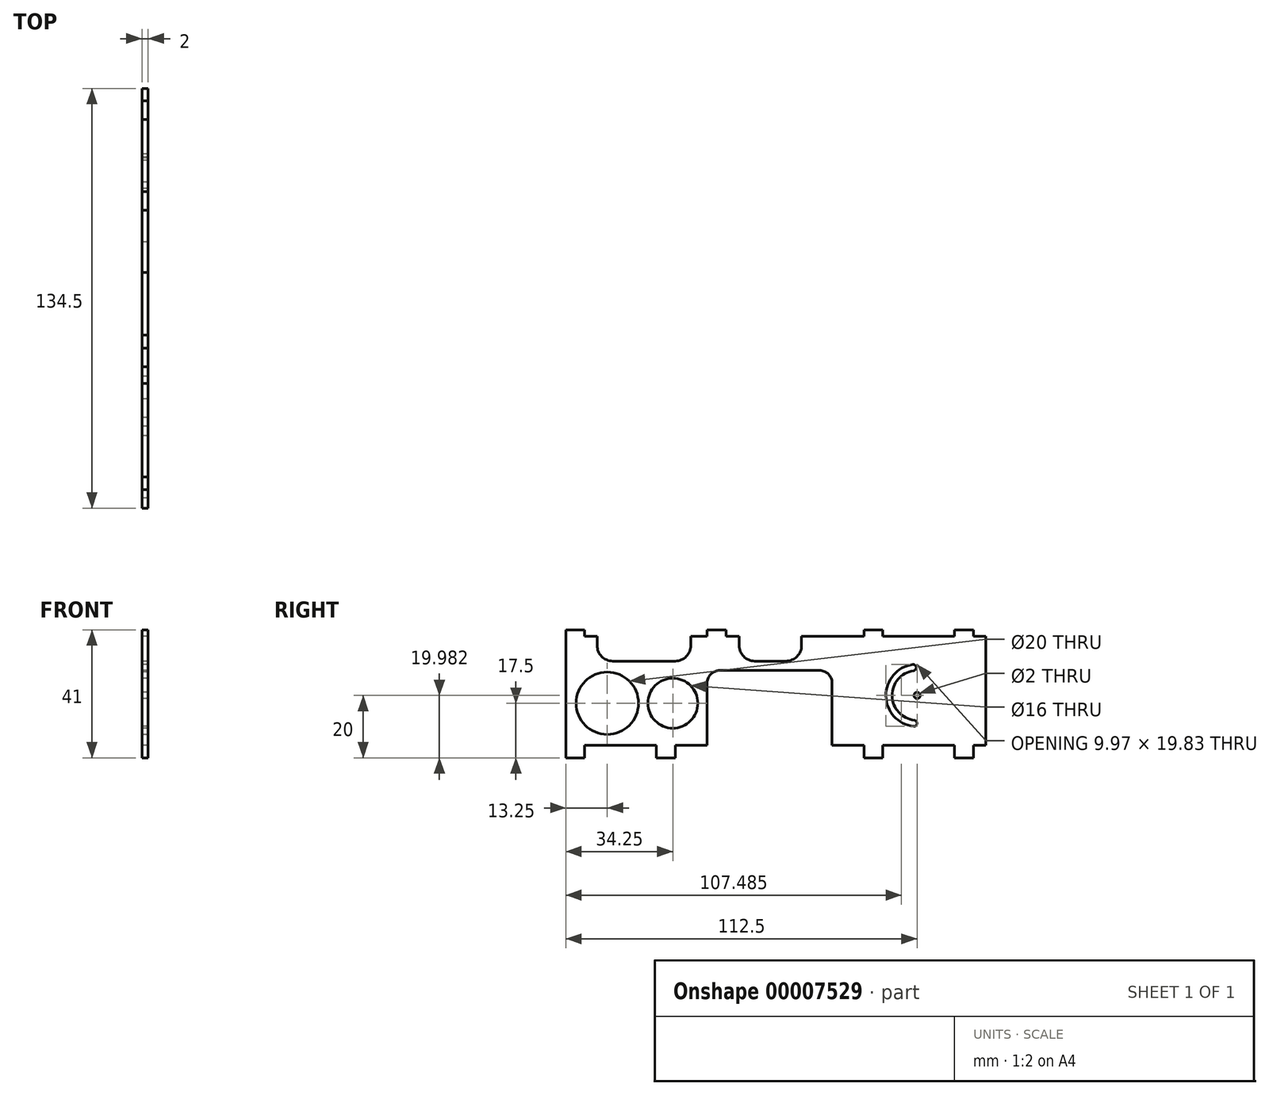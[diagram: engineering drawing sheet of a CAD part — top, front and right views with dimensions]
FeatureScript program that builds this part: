
annotation { "Feature Type Name" : "Feature", "Feature Type Description" : "" }
export const myFeature = defineFeature(function(context is Context, id is Id, definition is map)
    precondition{}
    {
        {
            var Q0;
            Q0=qCreatedBy(makeId("Right.planeOp"),FACE);
            var sketch = newSketch(context, id + "F0", { "sketchPlane" : qUnion([Q0])});
            skLineSegment(sketch, "E0.bottom", {"start": v(65.25, 0) * mm, "end": v(-65.25, 0) * mm});
            skLineSegment(sketch, "E0.top", {"start": v(65.25, 41) * mm, "end": v(-65.25, 41) * mm});
            skLineSegment(sketch, "E0.left", {"start": v(65.25, 0) * mm, "end": v(65.25, 41) * mm});
            skLineSegment(sketch, "E0.right", {"start": v(-65.25, 0) * mm, "end": v(-65.25, 41) * mm});
            skLineSegment(sketch, "E1.bottom", {"start": v(-59.25, 0) * mm, "end": v(-36.25, 0) * mm});
            skLineSegment(sketch, "E1.top", {"start": v(-59.25, 4) * mm, "end": v(-36.25, 4) * mm});
            skLineSegment(sketch, "E1.left", {"start": v(-59.25, 0) * mm, "end": v(-59.25, 4) * mm});
            skLineSegment(sketch, "E1.right", {"start": v(-36.25, 0) * mm, "end": v(-36.25, 4) * mm});
            skLineSegment(sketch, "E2.bottom", {"start": v(-20, 0) * mm, "end": v(20, 0) * mm});
            skLineSegment(sketch, "E2.top", {"start": v(-16, 28) * mm, "end": v(16, 28) * mm});
            skLineSegment(sketch, "E2.left", {"start": v(-20, 0) * mm, "end": v(-20, 24) * mm});
            skLineSegment(sketch, "E2.right", {"start": v(20, 0) * mm, "end": v(20, 24) * mm});
            skLineSegment(sketch, "E3.bottom", {"start": v(36.25, 0) * mm, "end": v(59.25, 0) * mm});
            skLineSegment(sketch, "E3.top", {"start": v(36.25, 4) * mm, "end": v(59.25, 4) * mm});
            skLineSegment(sketch, "E3.left", {"start": v(36.25, 0) * mm, "end": v(36.25, 4) * mm});
            skLineSegment(sketch, "E3.right", {"start": v(59.25, 0) * mm, "end": v(59.25, 4) * mm});
            skLineSegment(sketch, "E4.bottom", {"start": v(-30.25, 0) * mm, "end": v(-20, 0) * mm});
            skLineSegment(sketch, "E4.top", {"start": v(-30.25, 4) * mm, "end": v(-20, 4) * mm});
            skLineSegment(sketch, "E4.left", {"start": v(-30.25, 0) * mm, "end": v(-30.25, 4) * mm});
            skLineSegment(sketch, "E4.right", {"start": v(-20, 0) * mm, "end": v(-20, 4) * mm});
            skLineSegment(sketch, "E5.bottom", {"start": v(20, 0) * mm, "end": v(30.25, 0) * mm});
            skLineSegment(sketch, "E5.top", {"start": v(20, 4) * mm, "end": v(30.25, 4) * mm});
            skLineSegment(sketch, "E5.left", {"start": v(20, 0) * mm, "end": v(20, 4) * mm});
            skLineSegment(sketch, "E5.right", {"start": v(30.25, 0) * mm, "end": v(30.25, 4) * mm});
            skLineSegment(sketch, "E6.bottom", {"start": v(65.25, 41) * mm, "end": v(59.25, 41) * mm});
            skLineSegment(sketch, "E6.top", {"start": v(65.25, 39) * mm, "end": v(59.25, 39) * mm});
            skLineSegment(sketch, "E6.left", {"start": v(65.25, 41) * mm, "end": v(65.25, 39) * mm});
            skLineSegment(sketch, "E6.right", {"start": v(59.25, 41) * mm, "end": v(59.25, 39) * mm});
            skLineSegment(sketch, "E7.bottom", {"start": v(-20, 41) * mm, "end": v(-14, 41) * mm});
            skLineSegment(sketch, "E7.top", {"start": v(-20, 39) * mm, "end": v(-14, 39) * mm});
            skLineSegment(sketch, "E7.left", {"start": v(-20, 41) * mm, "end": v(-20, 39) * mm});
            skLineSegment(sketch, "E7.right", {"start": v(-14, 41) * mm, "end": v(-14, 39) * mm});
            skLineSegment(sketch, "E8.bottom", {"start": v(-65.25, 41) * mm, "end": v(-59.25, 41) * mm});
            skLineSegment(sketch, "E8.top", {"start": v(-65.25, 39) * mm, "end": v(-59.25, 39) * mm});
            skLineSegment(sketch, "E8.left", {"start": v(-65.25, 41) * mm, "end": v(-65.25, 39) * mm});
            skLineSegment(sketch, "E8.right", {"start": v(-59.25, 41) * mm, "end": v(-59.25, 39) * mm});
            skPoint(sketch, "E9.visualSharp", {"position": v(-20, 28) * mm});
            skArc(sketch, "E9.filletArc", {"start": v(-16, 28) * mm, "mid": v(-18.83, 26.83) * mm, "end": v(-20, 24) * mm});
            skPoint(sketch, "E10.visualSharp", {"position": v(20, 28) * mm});
            skArc(sketch, "E10.filletArc", {"start": v(20, 24) * mm, "mid": v(18.83, 26.83) * mm, "end": v(16, 28) * mm});
            skLineSegment(sketch, "E11.bottom", {"start": v(65.25, 39) * mm, "end": v(69.25, 39) * mm});
            skLineSegment(sketch, "E11.top", {"start": v(65.25, 4) * mm, "end": v(69.25, 4) * mm});
            skLineSegment(sketch, "E11.left", {"start": v(65.25, 39) * mm, "end": v(65.25, 4) * mm});
            skLineSegment(sketch, "E11.right", {"start": v(69.25, 39) * mm, "end": v(69.25, 4) * mm});
            skCircle(sketch, "E12", {"center": v(47.25, 20) * mm, "radius": 1 * mm});
            skArc(sketch, "E13", {"start": v(45.83, 29.9) * mm, "mid": v(37.25, 19.86) * mm, "end": v(46.11, 10.06) * mm});
            skArc(sketch, "E14.0", {"start": v(46.11, 27.92) * mm, "mid": v(39.25, 19.88) * mm, "end": v(46.34, 12.05) * mm});
            skArc(sketch, "E15", {"start": v(46.11, 10.06) * mm, "mid": v(47.22, 10.94) * mm, "end": v(46.34, 12.05) * mm});
            skArc(sketch, "E16", {"start": v(46.11, 27.92) * mm, "mid": v(46.96, 29.05) * mm, "end": v(45.83, 29.9) * mm});
            skLineSegment(sketch, "E17.bottom", {"start": v(-55.25, 41) * mm, "end": v(-25.25, 41) * mm});
            skLineSegment(sketch, "E17.top", {"start": v(-50.25, 31) * mm, "end": v(-30.25, 31) * mm});
            skLineSegment(sketch, "E17.left", {"start": v(-55.25, 41) * mm, "end": v(-55.25, 36) * mm});
            skLineSegment(sketch, "E17.right", {"start": v(-25.25, 41) * mm, "end": v(-25.25, 36) * mm});
            skLineSegment(sketch, "E18.bottom", {"start": v(-9.75, 41) * mm, "end": v(10.25, 41) * mm});
            skLineSegment(sketch, "E18.top", {"start": v(-4.75, 31) * mm, "end": v(5.25, 31) * mm});
            skLineSegment(sketch, "E18.left", {"start": v(-9.75, 41) * mm, "end": v(-9.75, 36) * mm});
            skLineSegment(sketch, "E18.right", {"start": v(10.25, 41) * mm, "end": v(10.25, 36) * mm});
            skPoint(sketch, "E19.visualSharp", {"position": v(-55.25, 31) * mm});
            skArc(sketch, "E19.filletArc", {"start": v(-55.25, 36) * mm, "mid": v(-53.79, 32.46) * mm, "end": v(-50.25, 31) * mm});
            skPoint(sketch, "E20.visualSharp", {"position": v(-25.25, 31) * mm});
            skArc(sketch, "E20.filletArc", {"start": v(-30.25, 31) * mm, "mid": v(-26.71, 32.46) * mm, "end": v(-25.25, 36) * mm});
            skPoint(sketch, "E21.visualSharp", {"position": v(-9.75, 31) * mm});
            skArc(sketch, "E21.filletArc", {"start": v(-9.75, 36) * mm, "mid": v(-8.29, 32.46) * mm, "end": v(-4.75, 31) * mm});
            skPoint(sketch, "E22.visualSharp", {"position": v(10.25, 31) * mm});
            skArc(sketch, "E22.filletArc", {"start": v(5.25, 31) * mm, "mid": v(8.79, 32.46) * mm, "end": v(10.25, 36) * mm});
            skCircle(sketch, "E23", {"center": v(-52, 17.5) * mm, "radius": 10 * mm});
            skLineSegment(sketch, "E24", {"start": v(-59.25, 39) * mm, "end": v(-20, 39) * mm});
            skLineSegment(sketch, "E25", {"start": v(-14, 39) * mm, "end": v(59.25, 39) * mm});
            skCircle(sketch, "E26", {"center": v(-31, 17.5) * mm, "radius": 8 * mm});
            skLineSegment(sketch, "E27.bottom", {"start": v(30.25, 39) * mm, "end": v(36.25, 39) * mm});
            skLineSegment(sketch, "E27.top", {"start": v(30.25, 41) * mm, "end": v(36.25, 41) * mm});
            skLineSegment(sketch, "E27.left", {"start": v(30.25, 39) * mm, "end": v(30.25, 41) * mm});
            skLineSegment(sketch, "E27.right", {"start": v(36.25, 39) * mm, "end": v(36.25, 41) * mm});
            skSolve(sketch);
        }
        {
            var Q0;
            Q0=makeQuery(id+"F0.imprint","IMPRINT",FACE,{"disambiguationData":[TD([[makeQuery(id+"F0.imprint","IMPRINT",EDGE,{"derivedFrom":sQuery(id+"F0.wireOp",EDGE,"E1.top")}),1.0]])]});
            var Q1;
            {var subQ4=sQuery(id+"F0.wireOp",EDGE,"E8.top");Q1=makeQuery(id+"F0.imprint","IMPRINT",FACE,{"disambiguationData":[TD([[makeQuery(id+"F0.imprint","IMPRINT",EDGE,{"derivedFrom":subQ4}),1.0]])]});}
            var Q2;
            Q2=makeQuery(id+"F0.imprint","IMPRINT",FACE,{"disambiguationData":[TD([[makeQuery(id+"F0.imprint","IMPRINT",EDGE,{"derivedFrom":sQuery(id+"F0.wireOp",EDGE,"E7.top")}),1.0]])]});
            var Q3;
            {var subQ4=sQuery(id+"F0.wireOp",EDGE,"E6.top");Q3=makeQuery(id+"F0.imprint","IMPRINT",FACE,{"disambiguationData":[TD([[makeQuery(id+"F0.imprint","IMPRINT",EDGE,{"derivedFrom":subQ4}),-1.0]])]});}
            var Q4;
            {var subQ2=sQuery(id+"F0.wireOp",EDGE,"E11.bottom");Q4=makeQuery(id+"F0.imprint","IMPRINT",FACE,{"disambiguationData":[TD([[makeQuery(id+"F0.imprint","IMPRINT",EDGE,{"derivedFrom":subQ2}),-1.0]])]});}
            var Q5;
            {var subQ2=sQuery(id+"F0.wireOp",EDGE,"E11.bottom");Q5=makeQuery(id+"F0.imprint","IMPRINT",FACE,{"disambiguationData":[TD([[makeQuery(id+"F0.imprint","IMPRINT",EDGE,{"derivedFrom":subQ2}),-1.0]])]});}
            var Q6;
            {var subQ0=sQuery(id+"F0.wireOp",EDGE,"E27.left");Q6=makeQuery(id+"F0.imprint","IMPRINT",FACE,{"disambiguationData":[TD([[makeQuery(id+"F0.imprint","IMPRINT",EDGE,{"derivedFrom":subQ0}),-1.0]])]});}
            extrude(context, id + "F1", {"entities" : qUnion([Q0, Q1, Q2, Q3, Q4, Q5, Q6]), "depth" : 2 * mm, "offsetDistance" : 25 * mm});
        }
    });
